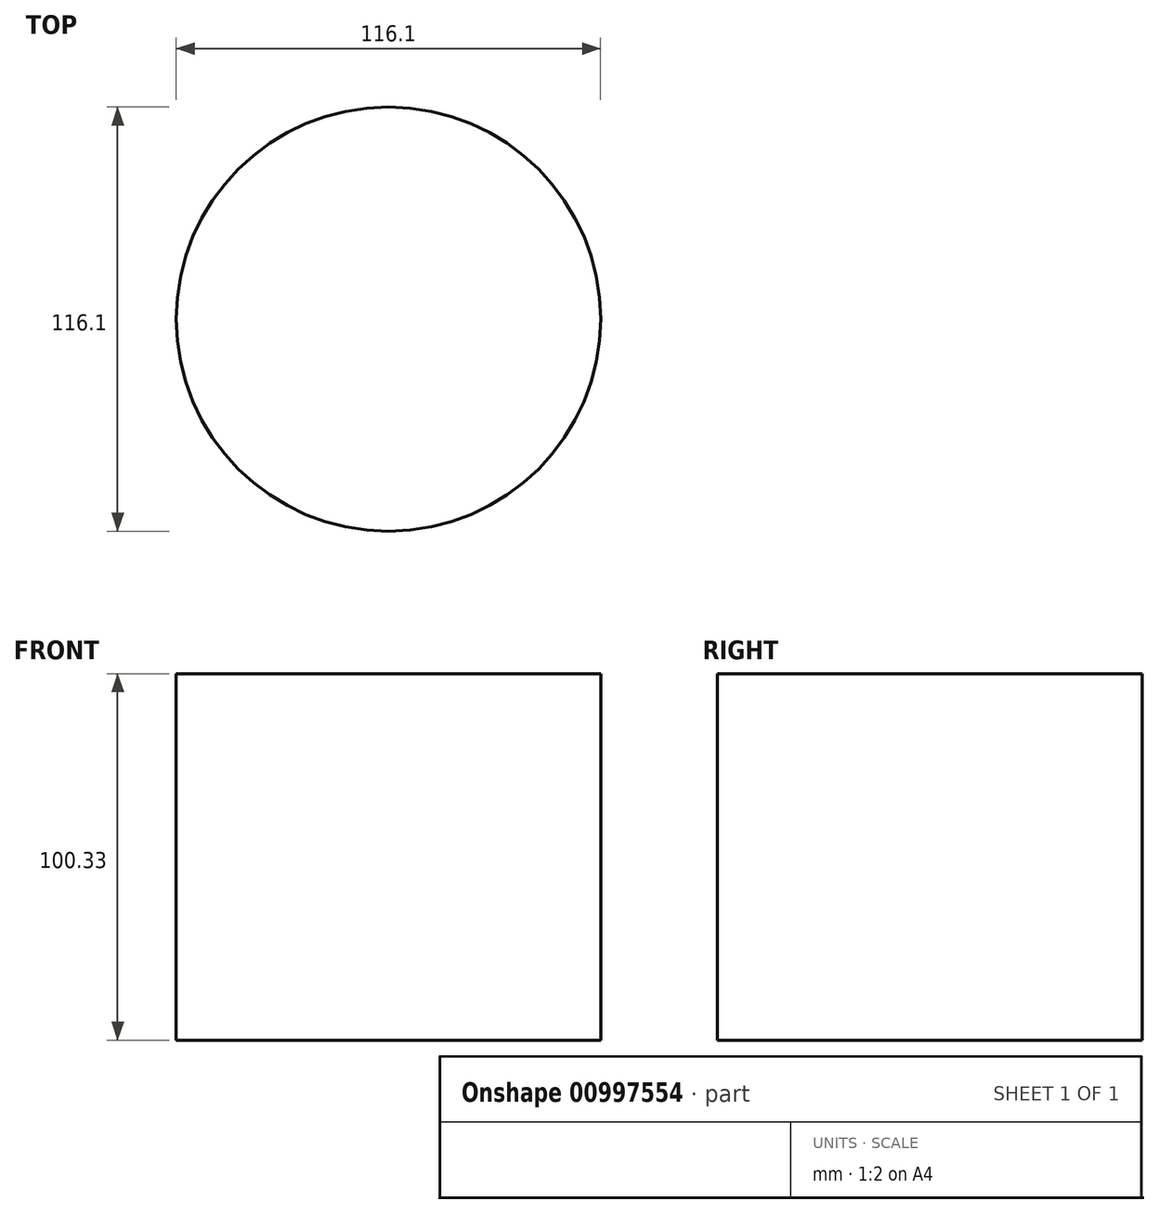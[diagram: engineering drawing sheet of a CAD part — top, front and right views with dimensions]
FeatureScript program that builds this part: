
annotation { "Feature Type Name" : "Feature", "Feature Type Description" : "" }
export const myFeature = defineFeature(function(context is Context, id is Id, definition is map)
    precondition{}
    {
        {
            var Q0;
            Q0=qCreatedBy(makeId("Top.planeOp"),FACE);
            var sketch = newSketch(context, id + "F0", { "sketchPlane" : qUnion([Q0])});
            skCircle(sketch, "E0", {"center": v(0, 0) * mm, "radius": 58.05 * mm});
            skSolve(sketch);
        }
        {
            var Q0;
            Q0=makeQuery(id+"F0.imprint","IMPRINT",FACE,{"disambiguationData":[TD([[makeQuery(id+"F0.imprint","IMPRINT",EDGE,{"derivedFrom":sQuery(id+"F0.wireOp",EDGE,"E0")}),1.0]])]});
            extrude(context, id + "F1", {"entities" : qUnion([Q0]), "depth" : 100.33 * mm, "offsetDistance" : 25.4 * mm});
        }
    });
